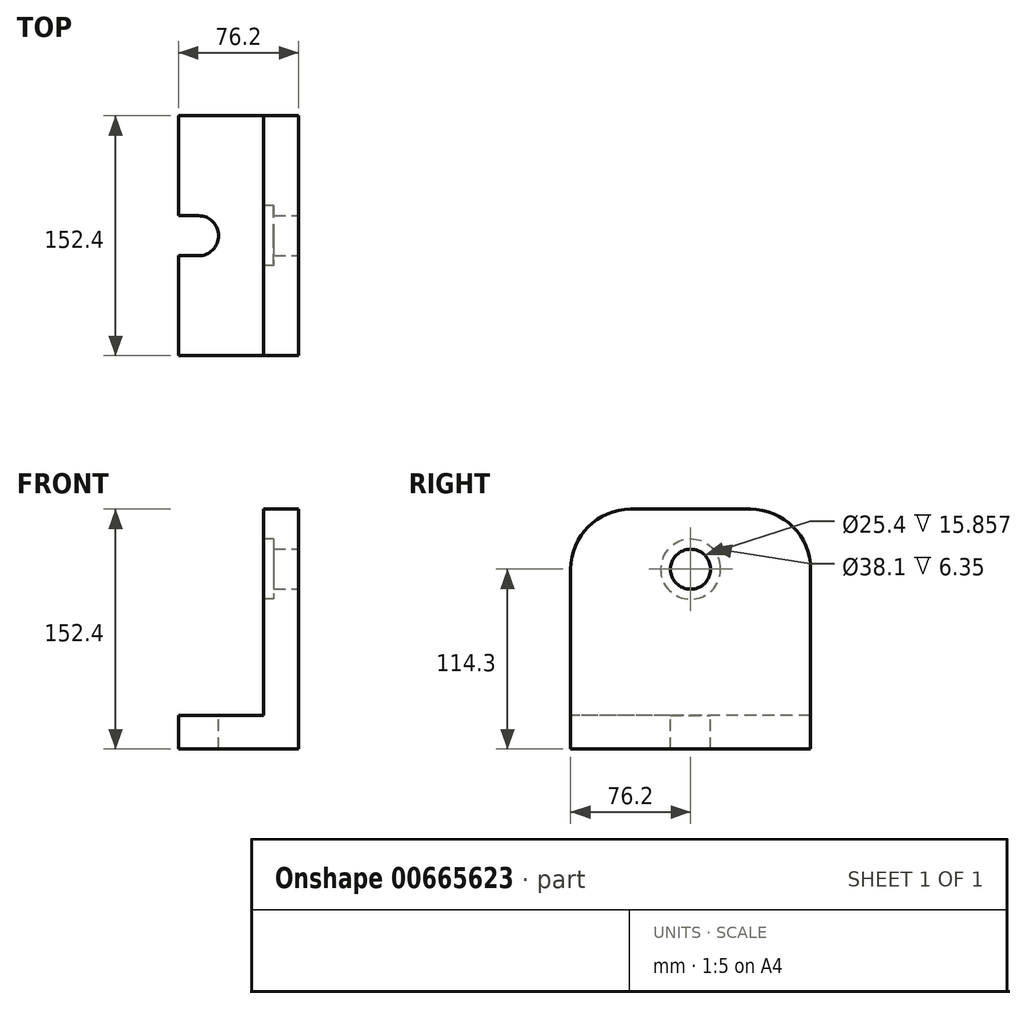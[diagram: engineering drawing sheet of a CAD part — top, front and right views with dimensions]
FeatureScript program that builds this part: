
annotation { "Feature Type Name" : "Feature", "Feature Type Description" : "" }
export const myFeature = defineFeature(function(context is Context, id is Id, definition is map)
    precondition{}
    {
        {
            var Q0;
            Q0=qCreatedBy(makeId("Front.planeOp"),FACE);
            var sketch = newSketch(context, id + "F0", { "sketchPlane" : qUnion([Q0])});
            skLineSegment(sketch, "E0", {"start": v(0, 0) * mm, "end": v(0, 152.4) * mm});
            skLineSegment(sketch, "E1", {"start": v(-22.2, 152.4) * mm, "end": v(-22.2, 21.34) * mm});
            skLineSegment(sketch, "E2", {"start": v(-22.2, 21.34) * mm, "end": v(-76.2, 21.34) * mm});
            skLineSegment(sketch, "E3", {"start": v(-76.2, 21.34) * mm, "end": v(-76.2, 0) * mm});
            skLineSegment(sketch, "E4", {"start": v(-76.2, 0) * mm, "end": v(0, 0) * mm});
            skLineSegment(sketch, "E5", {"start": v(0, 152.4) * mm, "end": v(-22.2, 152.4) * mm});
            skSolve(sketch);
        }
        {
            var Q0;
            Q0=makeQuery(id+"F0.imprint","IMPRINT",FACE,{"disambiguationData":[TD([[makeQuery(id+"F0.imprint","IMPRINT",EDGE,{"derivedFrom":sQuery(id+"F0.wireOp",EDGE,"E0")}),1.0]])]});
            extrude(context, id + "F1", {"entities" : qUnion([Q0]), "oppositeDirection" : true, "depth" : 76.2 * mm, "offsetDistance" : 25.4 * mm});
        }
        {
            var Q0;
            Q0=makeQuery(id+"F1.opExtrude","CAP_FACE",FACE,{"disambiguationData":[OSD([sQuery(id+"F0.wireOp",EDGE,"E0"),sQuery(id+"F0.wireOp",EDGE,"E1"),sQuery(id+"F0.wireOp",EDGE,"E2"),sQuery(id+"F0.wireOp",EDGE,"E3"),sQuery(id+"F0.wireOp",EDGE,"E4"),sQuery(id+"F0.wireOp",EDGE,"E5")])],"isStart":true});
            extrude(context, id + "F2", {"entities" : qUnion([Q0]), "operationType" : NewBodyOperationType.ADD, "depth" : 76.2 * mm, "offsetDistance" : 25.4 * mm});
        }
        {
            var Q0;
            {var subQ0=sQuery(id+"F0.wireOp",EDGE,"E0");Q0=makeQuery(id+"F2.boolean.opBoolean","MERGE",FACE,{"derivedFrom":[makeQuery(id+"F1.opExtrude","SWEPT_FACE",FACE,{"disambiguationData":[OSD([subQ0])]}),makeQuery(id+"F2.opExtrude","SWEPT_FACE",FACE,{"disambiguationData":[OSD([subQ0])]})]});}
            var sketch = newSketch(context, id + "F3", { "sketchPlane" : qUnion([Q0])});
            skCircle(sketch, "E6", {"center": v(0, 114.3) * mm, "radius": 12.7 * mm});
            skPoint(sketch, "E6.centerSnap0", {"position": v(0, 152.4) * mm});
            skSolve(sketch);
        }
        {
            var Q0;
            Q0=makeQuery(id+"F3.imprint","IMPRINT",FACE,{"disambiguationData":[TD([[makeQuery(id+"F3.imprint","IMPRINT",EDGE,{"derivedFrom":sQuery(id+"F3.wireOp",EDGE,"E6")}),1.0]])]});
            extrude(context, id + "F4", {"entities" : qUnion([Q0]), "operationType" : NewBodyOperationType.REMOVE, "endBound" : BoundingType.THROUGH_ALL, "oppositeDirection" : true, "depth" : 25.4 * mm, "offsetDistance" : 25.4 * mm});
        }
        {
            var Q0;
            {var subQ0=sQuery(id+"F0.wireOp",EDGE,"E2");Q0=makeQuery(id+"F2.boolean.opBoolean","MERGE",FACE,{"derivedFrom":[makeQuery(id+"F1.opExtrude","SWEPT_FACE",FACE,{"disambiguationData":[OSD([subQ0])]}),makeQuery(id+"F2.opExtrude","SWEPT_FACE",FACE,{"disambiguationData":[OSD([subQ0])]})]});}
            var sketch = newSketch(context, id + "F5", { "sketchPlane" : qUnion([Q0])});
            skLineSegment(sketch, "E7.bottom", {"start": v(-76.2, 12.7) * mm, "end": v(-63.5, 12.7) * mm});
            skLineSegment(sketch, "E7.top", {"start": v(-76.2, -12.7) * mm, "end": v(-63.5, -12.7) * mm});
            skLineSegment(sketch, "E7.left", {"start": v(-76.2, 12.7) * mm, "end": v(-76.2, -12.7) * mm});
            skPoint(sketch, "E7.middle", {"position": v(-69.85, 0) * mm});
            skArc(sketch, "E8", {"start": v(-63.5, 12.7) * mm, "mid": v(-50.8, 0) * mm, "end": v(-63.5, -12.7) * mm});
            skSolve(sketch);
        }
        {
            var Q0;
            Q0=makeQuery(id+"F5.imprint","IMPRINT",FACE,{"disambiguationData":[TD([[makeQuery(id+"F5.imprint","IMPRINT",EDGE,{"derivedFrom":sQuery(id+"F5.wireOp",EDGE,"E7.bottom")}),-1.0]])]});
            extrude(context, id + "F6", {"entities" : qUnion([Q0]), "operationType" : NewBodyOperationType.REMOVE, "oppositeDirection" : true, "depth" : 25.4 * mm, "offsetDistance" : 25.4 * mm});
        }
        {
            var Q0;
            Q0=makeQuery(id+"F2.opExtrude","CAP_EDGE",EDGE,{"disambiguationData":[OSD([sQuery(id+"F0.wireOp",EDGE,"E5")])],"isStart":false});
            var Q1;
            Q1=makeQuery(id+"F1.opExtrude","CAP_EDGE",EDGE,{"disambiguationData":[OSD([sQuery(id+"F0.wireOp",EDGE,"E5")])],"isStart":false});
            fillet(context, id + "F7", {"entities" : qUnion([Q0, Q1]), "radius" : 38.1 * mm, "tangentPropagation" : true, "allowEdgeOverflow" : false});
        }
        {
            var Q0;
            {var subQ0=sQuery(id+"F0.wireOp",EDGE,"E1");Q0=makeQuery(id+"F2.boolean.opBoolean","MERGE",FACE,{"derivedFrom":[makeQuery(id+"F1.opExtrude","SWEPT_FACE",FACE,{"disambiguationData":[OSD([subQ0])]}),makeQuery(id+"F2.opExtrude","SWEPT_FACE",FACE,{"disambiguationData":[OSD([subQ0])]})]});}
            var sketch = newSketch(context, id + "F8", { "sketchPlane" : qUnion([Q0])});
            skCircle(sketch, "E9", {"center": v(0, 114.3) * mm, "radius": 19.05 * mm});
            skSolve(sketch);
        }
        {
            var Q0;
            Q0 = qSketchRegion(id + "F8", true);
            extrude(context, id + "F9", {"entities" : qUnion([Q0]), "operationType" : NewBodyOperationType.REMOVE, "oppositeDirection" : true, "depth" : 6.35 * mm, "offsetDistance" : 25.4 * mm});
        }
        {
            var Q0;
            Q0=makeQuery(id+"F2.opExtrude","CAP_FACE",FACE,{"disambiguationData":[OSD([sQuery(id+"F0.wireOp",EDGE,"E0"),sQuery(id+"F0.wireOp",EDGE,"E1"),sQuery(id+"F0.wireOp",EDGE,"E2"),sQuery(id+"F0.wireOp",EDGE,"E3"),sQuery(id+"F0.wireOp",EDGE,"E4"),sQuery(id+"F0.wireOp",EDGE,"E5")])],"isStart":false});
            cPlane(context, id + "F10", {"entities" : qUnion([Q0]), "cplaneType" : CPlaneType.OFFSET, "offset" : 44.45 * mm, "width" : 152.4 * mm, "height" : 152.4 * mm});
        }
    });
